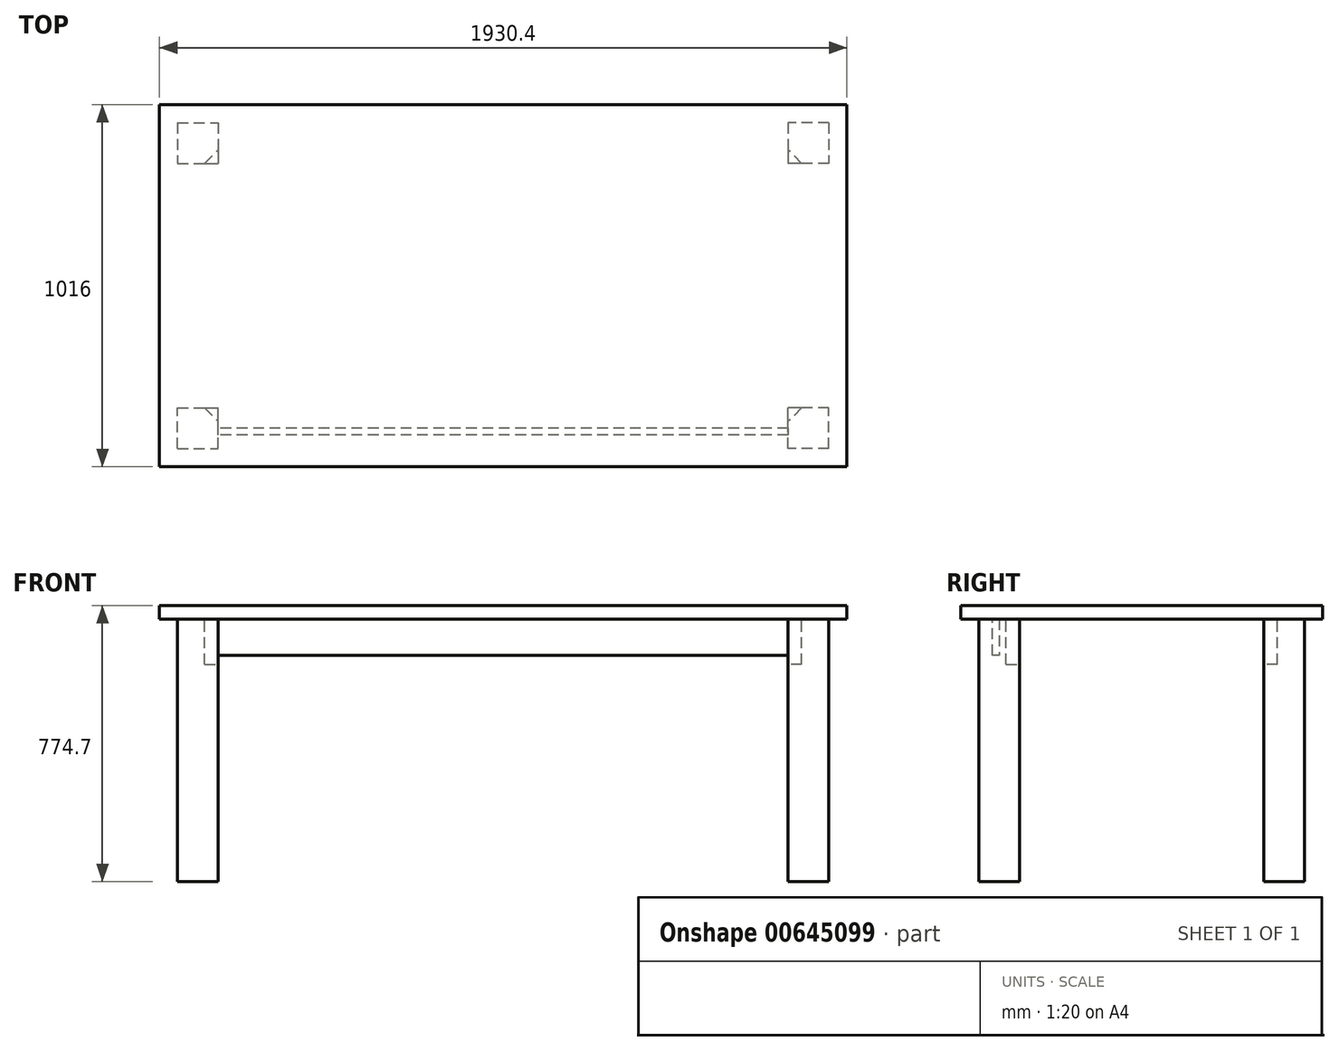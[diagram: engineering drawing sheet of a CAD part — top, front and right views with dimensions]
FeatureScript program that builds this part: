
annotation { "Feature Type Name" : "Feature", "Feature Type Description" : "" }
export const myFeature = defineFeature(function(context is Context, id is Id, definition is map)
    precondition{}
    {
        {
            var Q0;
            Q0=qCreatedBy(makeId("Top.planeOp"),FACE);
            var sketch = newSketch(context, id + "F0", { "sketchPlane" : qUnion([Q0])});
            skLineSegment(sketch, "E0.bottom", {"start": v(0, 0) * mm, "end": v(1930.4, 0) * mm});
            skLineSegment(sketch, "E0.top", {"start": v(0, 1016) * mm, "end": v(1930.4, 1016) * mm});
            skLineSegment(sketch, "E0.left", {"start": v(0, 0) * mm, "end": v(0, 1016) * mm});
            skLineSegment(sketch, "E0.right", {"start": v(1930.4, 0) * mm, "end": v(1930.4, 1016) * mm});
            skSolve(sketch);
        }
        {
            var Q0;
            Q0 = qSketchRegion(id + "F0", true);
            extrude(context, id + "F1", {"entities" : qUnion([Q0]), "oppositeDirection" : true, "depth" : 38.1 * mm, "offsetDistance" : 25.4 * mm});
        }
        {
            var Q0;
            Q0=qCreatedBy(makeId("Front.planeOp"),FACE);
            cPlane(context, id + "F2", {"entities" : qUnion([Q0]), "cplaneType" : CPlaneType.OFFSET, "offset" : 508 * mm, "oppositeDirection" : true, "width" : 152.4 * mm, "height" : 152.4 * mm});
        }
        {
            var Q0;
            Q0=makeQuery(id+"F1.opExtrude","CAP_FACE",FACE,{"disambiguationData":[OSD([sQuery(id+"F0.wireOp",EDGE,"E0.bottom"),sQuery(id+"F0.wireOp",EDGE,"E0.top"),sQuery(id+"F0.wireOp",EDGE,"E0.left"),sQuery(id+"F0.wireOp",EDGE,"E0.right")])],"isStart":false});
            var sketch = newSketch(context, id + "F3", { "sketchPlane" : qUnion([Q0])});
            skLineSegment(sketch, "E1.bottom", {"start": v(50.8, -50.8) * mm, "end": v(165.1, -50.8) * mm});
            skLineSegment(sketch, "E1.top", {"start": v(50.8, -165.1) * mm, "end": v(165.1, -165.1) * mm});
            skLineSegment(sketch, "E1.left", {"start": v(50.8, -50.8) * mm, "end": v(50.8, -165.1) * mm});
            skLineSegment(sketch, "E1.right", {"start": v(165.1, -50.8) * mm, "end": v(165.1, -165.1) * mm});
            skSolve(sketch);
        }
        {
            var Q0;
            Q0 = qSketchRegion(id + "F3", true);
            extrude(context, id + "F4", {"entities" : qUnion([Q0]), "depth" : 736.6 * mm, "offsetDistance" : 25.4 * mm});
        }
        {
            var Q0;
            Q0=qCreatedBy(makeId("Right.planeOp"),FACE);
            cPlane(context, id + "F5", {"entities" : qUnion([Q0]), "cplaneType" : CPlaneType.OFFSET, "offset" : 965.2 * mm, "width" : 152.4 * mm, "height" : 152.4 * mm});
        }
        {
            var Q0;
            Q0=makeQuery(id+"F4.opExtrude","CAP_FACE",FACE,{"disambiguationData":[OSD([sQuery(id+"F3.wireOp",EDGE,"E1.bottom"),sQuery(id+"F3.wireOp",EDGE,"E1.top"),sQuery(id+"F3.wireOp",EDGE,"E1.left"),sQuery(id+"F3.wireOp",EDGE,"E1.right")])],"isStart":true});
            var sketch = newSketch(context, id + "F6", { "sketchPlane" : qUnion([Q0])});
            skLineSegment(sketch, "E2.0", {"start": v(127, 165.1) * mm, "end": v(165.1, 165.1) * mm});
            skLineSegment(sketch, "E2.1", {"start": v(165.1, 127) * mm, "end": v(165.1, 165.1) * mm});
            skLineSegment(sketch, "E3", {"start": v(127, 165.1) * mm, "end": v(165.1, 127) * mm});
            skPoint(sketch, "E4.orphan", {"position": v(165.1, 50.8) * mm});
            skPoint(sketch, "E5.orphan", {"position": v(50.8, 165.1) * mm});
            skSolve(sketch);
        }
        {
            var Q0;
            Q0 = qSketchRegion(id + "F6", true);
            extrude(context, id + "F7", {"entities" : qUnion([Q0]), "operationType" : NewBodyOperationType.REMOVE, "oppositeDirection" : true, "depth" : 127 * mm, "offsetDistance" : 25.4 * mm});
        }
        {
            var Q0;
            Q0=makeQuery(id+"F4.opExtrude","SWEPT_BODY",BODY,{"disambiguationData":[OSD([sQuery(id+"F3.wireOp",EDGE,"E1.bottom"),sQuery(id+"F3.wireOp",EDGE,"E1.top"),sQuery(id+"F3.wireOp",EDGE,"E1.left"),sQuery(id+"F3.wireOp",EDGE,"E1.right")])]});
            var Q1;
            Q1=qCreatedBy(id+"F2.planeOp",FACE);
            mirror(context, id + "F8", {"entities" : qUnion([Q0]), "mirrorPlane" : qUnion([Q1])});
        }
        {
            var Q0;
            Q0=makeQuery(id+"F8.opPattern","COPY",BODY,{"derivedFrom":makeQuery(id+"F4.opExtrude","SWEPT_BODY",BODY,{"disambiguationData":[OSD([sQuery(id+"F3.wireOp",EDGE,"E1.bottom"),sQuery(id+"F3.wireOp",EDGE,"E1.top"),sQuery(id+"F3.wireOp",EDGE,"E1.left"),sQuery(id+"F3.wireOp",EDGE,"E1.right")])]}),"instanceName":"1"});
            var Q1;
            Q1=makeQuery(id+"F4.opExtrude","SWEPT_BODY",BODY,{"disambiguationData":[OSD([sQuery(id+"F3.wireOp",EDGE,"E1.bottom"),sQuery(id+"F3.wireOp",EDGE,"E1.top"),sQuery(id+"F3.wireOp",EDGE,"E1.left"),sQuery(id+"F3.wireOp",EDGE,"E1.right")])]});
            var Q2;
            Q2=qCreatedBy(id+"F5.planeOp",FACE);
            mirror(context, id + "F9", {"entities" : qUnion([Q0, Q1]), "mirrorPlane" : qUnion([Q2])});
        }
        {
            var Q0;
            Q0=makeQuery(id+"F4.opExtrude","SWEPT_FACE",FACE,{"disambiguationData":[OSD([sQuery(id+"F3.wireOp",EDGE,"E1.right")])]});
            var sketch = newSketch(context, id + "F10", { "sketchPlane" : qUnion([Q0])});
            skLineSegment(sketch, "E6.0", {"start": v(88.9, -38.1) * mm, "end": v(107.95, -38.1) * mm});
            skLineSegment(sketch, "E7", {"start": v(88.9, -38.1) * mm, "end": v(88.9, -139.7) * mm});
            skLineSegment(sketch, "E8", {"start": v(88.9, -139.7) * mm, "end": v(107.95, -139.7) * mm});
            skLineSegment(sketch, "E9", {"start": v(107.95, -139.7) * mm, "end": v(107.95, -38.1) * mm});
            skPoint(sketch, "E10.orphan", {"position": v(127, -38.1) * mm});
            skPoint(sketch, "E11.orphan", {"position": v(50.8, -38.1) * mm});
            skSolve(sketch);
        }
        {
            var Q0;
            Q0 = qSketchRegion(id + "F10", true);
            extrude(context, id + "F11", {"entities" : qUnion([Q0]), "endBound" : BoundingType.UP_TO_NEXT, "depth" : 25.4 * mm, "offsetDistance" : 25.4 * mm});
        }
    });
